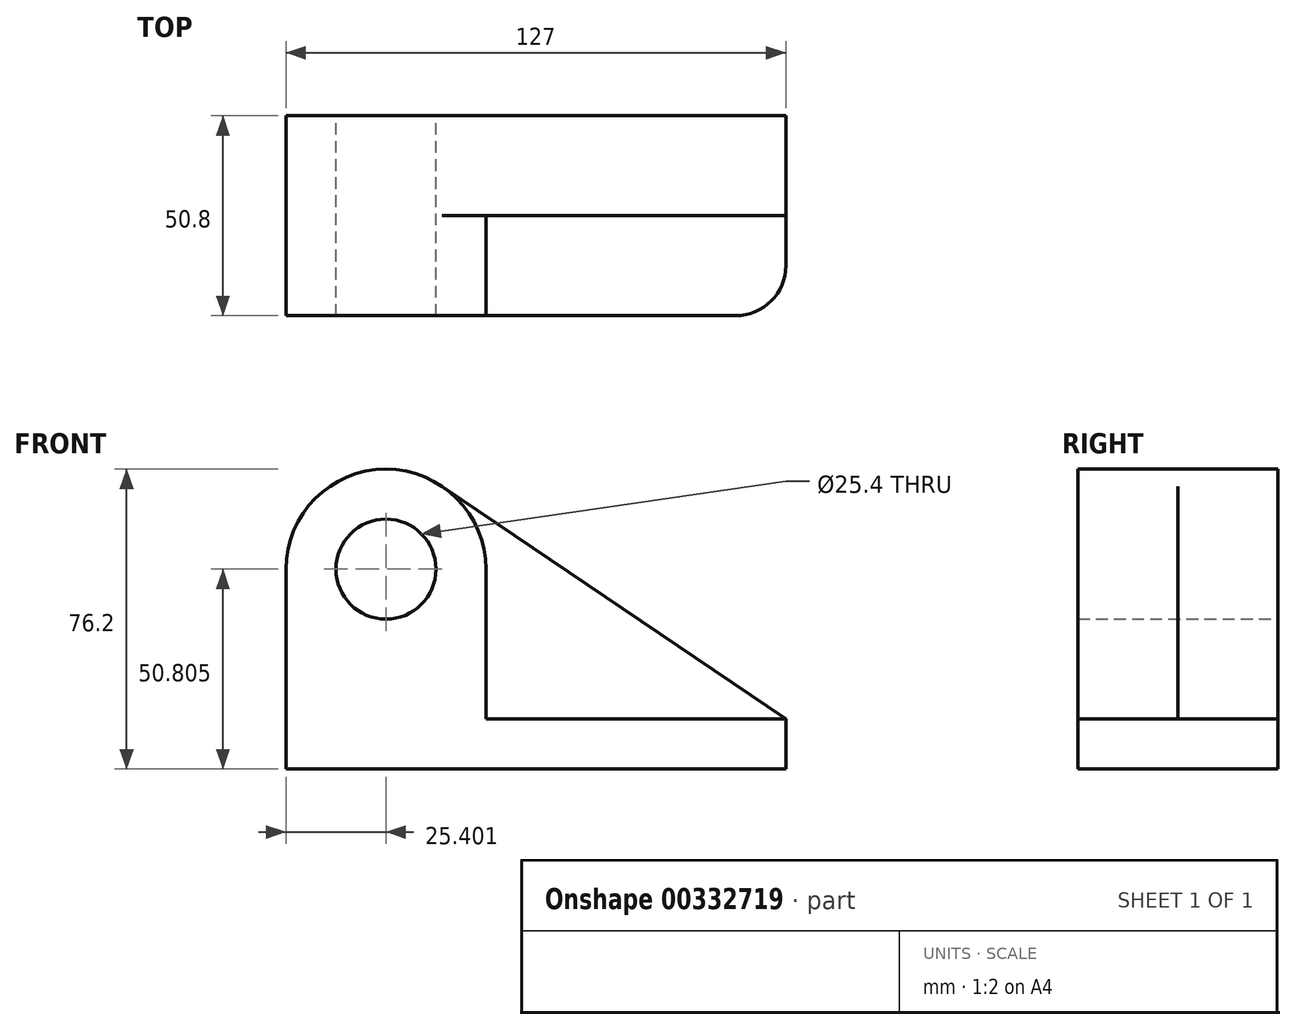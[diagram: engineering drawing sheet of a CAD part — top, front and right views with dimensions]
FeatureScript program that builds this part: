
annotation { "Feature Type Name" : "Feature", "Feature Type Description" : "" }
export const myFeature = defineFeature(function(context is Context, id is Id, definition is map)
    precondition{}
    {
        {
            var Q0;
            Q0=qCreatedBy(makeId("Front.planeOp"),FACE);
            var sketch = newSketch(context, id + "F0", { "sketchPlane" : qUnion([Q0])});
            skCircle(sketch, "E0", {"center": v(-39.32, 39.67) * mm, "radius": 12.7 * mm});
            skArc(sketch, "E1", {"start": v(-25.08, 60.7) * mm, "mid": v(-51.23, 62.11) * mm, "end": v(-64.72, 39.67) * mm});
            skLineSegment(sketch, "E2", {"start": v(-64.72, 39.67) * mm, "end": v(-64.72, -11.13) * mm});
            skLineSegment(sketch, "E3", {"start": v(62.28, -11.13) * mm, "end": v(-64.72, -11.13) * mm});
            skLineSegment(sketch, "E4", {"start": v(62.28, 1.57) * mm, "end": v(62.28, -11.13) * mm});
            skLineSegment(sketch, "E5", {"start": v(62.28, 1.57) * mm, "end": v(-25.08, 60.7) * mm});
            skSolve(sketch);
        }
        {
            var Q0;
            Q0=makeQuery(id+"F0.imprint","IMPRINT",FACE,{"disambiguationData":[TD([[makeQuery(id+"F0.imprint","IMPRINT",EDGE,{"derivedFrom":sQuery(id+"F0.wireOp",EDGE,"E0")}),-1.0]])]});
            extrude(context, id + "F1", {"entities" : qUnion([Q0]), "depth" : 25.4 * mm});
        }
        {
            var Q0;
            Q0=makeQuery(id+"F1.opExtrude","CAP_FACE",FACE,{"disambiguationData":[OSD([sQuery(id+"F0.wireOp",EDGE,"E0"),sQuery(id+"F0.wireOp",EDGE,"E1"),sQuery(id+"F0.wireOp",EDGE,"E2"),sQuery(id+"F0.wireOp",EDGE,"E3"),sQuery(id+"F0.wireOp",EDGE,"E4"),sQuery(id+"F0.wireOp",EDGE,"E5")])],"isStart":false});
            var sketch = newSketch(context, id + "F2", { "sketchPlane" : qUnion([Q0])});
            skCircle(sketch, "E6", {"center": v(-39.32, 39.67) * mm, "radius": 12.7 * mm});
            skLineSegment(sketch, "E7.left", {"start": v(62.28, 1.57) * mm, "end": v(62.28, 1.57) * mm});
            skLineSegment(sketch, "E7.right", {"start": v(-64.72, 1.57) * mm, "end": v(-64.72, 1.57) * mm});
            skArc(sketch, "E8", {"start": v(-13.92, 39.67) * mm, "mid": v(-39.32, 65.07) * mm, "end": v(-64.72, 39.67) * mm});
            skLineSegment(sketch, "E9.bottom", {"start": v(62.28, 1.57) * mm, "end": v(-13.92, 1.57) * mm});
            skLineSegment(sketch, "E9.top", {"start": v(62.28, -11.13) * mm, "end": v(-64.72, -11.13) * mm});
            skLineSegment(sketch, "E9.left", {"start": v(62.28, 1.57) * mm, "end": v(62.28, -11.13) * mm});
            skLineSegment(sketch, "E9.right", {"start": v(-64.72, 1.57) * mm, "end": v(-64.72, -11.13) * mm});
            skLineSegment(sketch, "E10", {"start": v(-64.72, 39.67) * mm, "end": v(-64.72, 1.57) * mm});
            skLineSegment(sketch, "E11", {"start": v(-13.92, 39.67) * mm, "end": v(-13.92, 1.57) * mm});
            skSolve(sketch);
        }
        {
            var Q0;
            Q0=makeQuery(id+"F2.imprint","IMPRINT",FACE,{"disambiguationData":[TD([[makeQuery(id+"F2.imprint","IMPRINT",EDGE,{"derivedFrom":sQuery(id+"F2.wireOp",EDGE,"E6")}),-1.0]])]});
            extrude(context, id + "F3", {"entities" : qUnion([Q0]), "operationType" : NewBodyOperationType.ADD, "depth" : 25.4 * mm});
        }
        {
            var Q0;
            Q0=makeQuery(id+"F3.opExtrude","CAP_EDGE",EDGE,{"disambiguationData":[OSD([sQuery(id+"F2.wireOp",EDGE,"E9.left")])],"isStart":false});
            fillet(context, id + "F4", {"entities" : qUnion([Q0]), "radius" : 12.7 * mm, "tangentPropagation" : true, "allowEdgeOverflow" : false});
        }
    });
